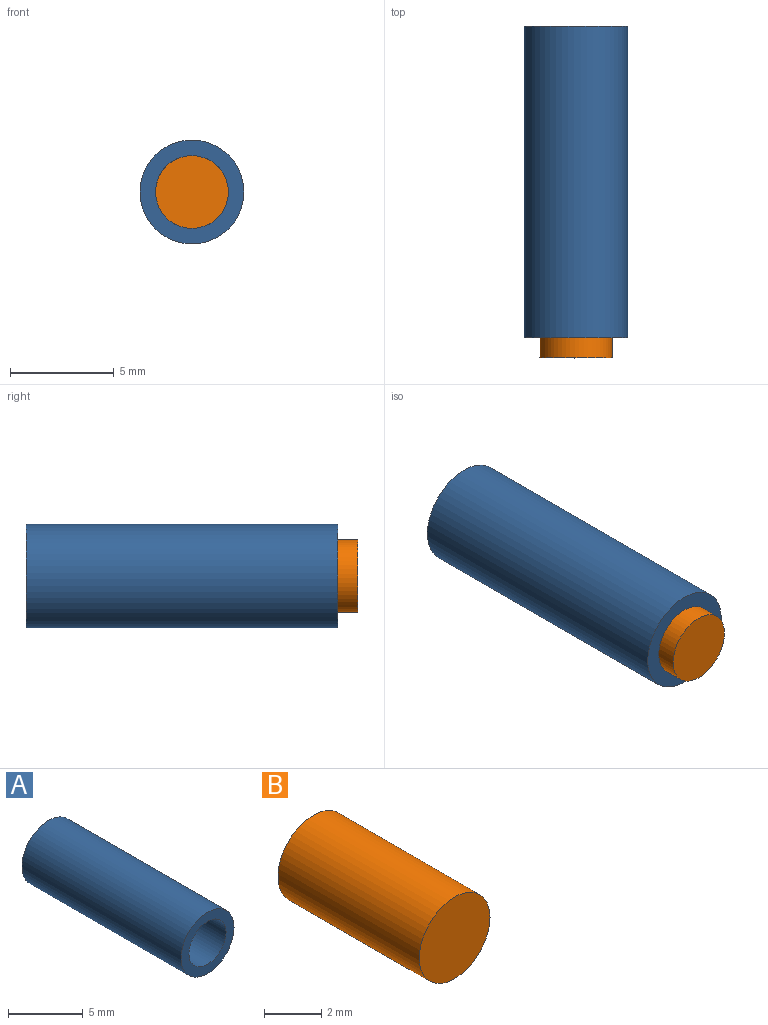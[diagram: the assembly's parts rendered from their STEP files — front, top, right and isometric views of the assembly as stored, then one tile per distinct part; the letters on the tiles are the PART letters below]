
ASSEMBLY  parts=2 mates=1
PART A: 4 faces, bbox 5x15x5 mm
  f0: cylinder r=2.5mm len=15mm, axis (0,1,0), area 235.6mm2, adj f1,f2
  f1: plane 5x5mm, normal (0,-1,0), area 10mm2, adj f0,f3
  f2: plane 5x5mm, normal (0,1,0), area 10mm2, adj f0,f3
  f3: cylinder r=1.75mm len=15mm, axis (0,-1,0), area 164.9mm2, adj f1,f2
PART B: 3 faces, bbox 3.5x7x3.5 mm
  f0: cylinder r=1.75mm len=7mm, axis (0,1,0), area 77mm2, adj f1,f2
  f1: plane 3.5x3.5mm, normal (0,-1,0), area 9.6mm2, adj f0
  f2: plane 3.5x3.5mm, normal (0,1,0), area 9.6mm2, adj f0
PLACE A t=(-3.68,4.68,-2.51)mm
PLACE B t=(-3.68,-4.3,-2.51)mm
MATE slider B.f0 <-> A.f0  axis (0,-1,0) through (-3.68,-11.3,-2.51)mm
